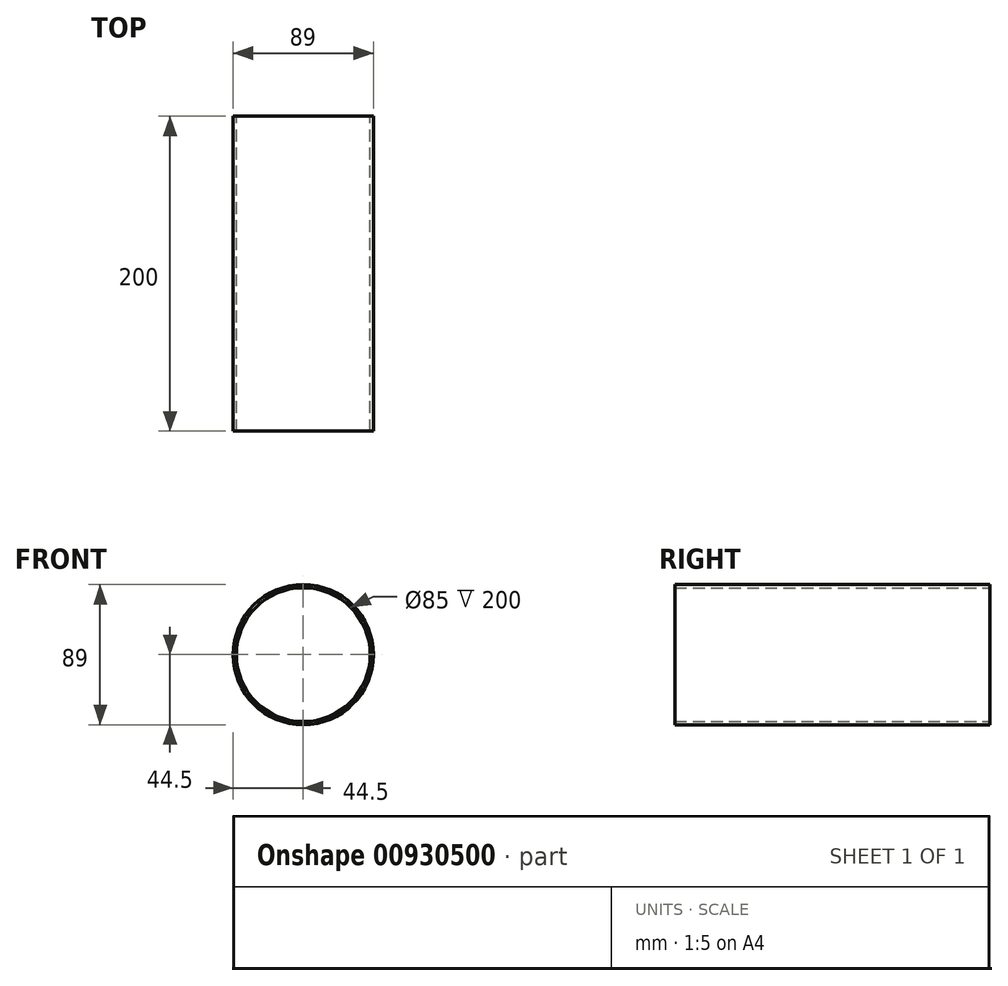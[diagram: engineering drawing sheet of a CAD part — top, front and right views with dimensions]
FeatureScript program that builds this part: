
annotation { "Feature Type Name" : "Feature", "Feature Type Description" : "" }
export const myFeature = defineFeature(function(context is Context, id is Id, definition is map)
    precondition{}
    {
        {
            var Q0;
            Q0=qCreatedBy(makeId("Front.planeOp"),FACE);
            var sketch = newSketch(context, id + "F0", { "sketchPlane" : qUnion([Q0])});
            skCircle(sketch, "E0", {"center": v(0, 0) * mm, "radius": 44.5 * mm});
            skCircle(sketch, "E1.0", {"center": v(0, 0) * mm, "radius": 42.5 * mm});
            skSolve(sketch);
        }
        {
            var Q0;
            Q0 = qSketchRegion(id + "F0", true);
            extrude(context, id + "F1", {"entities" : qUnion([Q0]), "depth" : 200 * mm, "offsetDistance" : 25 * mm});
        }
    });
